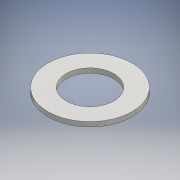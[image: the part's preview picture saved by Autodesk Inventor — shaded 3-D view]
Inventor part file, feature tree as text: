
AUTODESK INVENTOR PART (.ipt)
format: ipt  version: 2016 (Build 200138000, 138)  size: 96,256 bytes
history: native  units: mm
features: other x1, extrude x1, sketch x1
ambient origin geometry x8: Origin, YZ Plane, XZ Plane, XY Plane, X Axis, Y Axis, Z Axis, Center Point
bodies: Body1 (feature_tree)
feature tree (3):
  other  "ソリッド1"
  extrude  "押し出し1"  Depth=10.2mm
  sketch  "スケッチ1"
